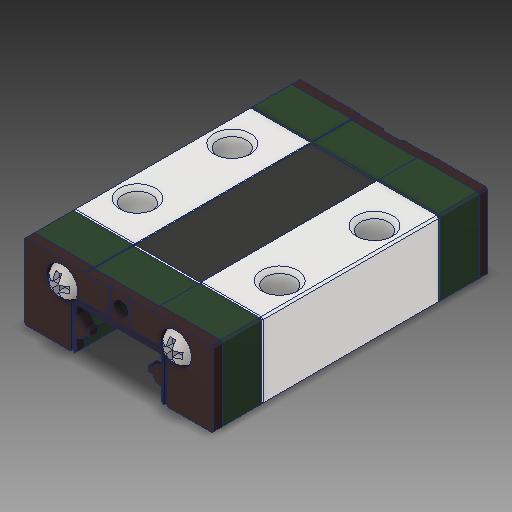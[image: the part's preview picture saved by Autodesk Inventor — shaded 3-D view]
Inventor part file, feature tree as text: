
AUTODESK INVENTOR PART (.ipt)
format: ipt  version: 2017.3 (Build 213256000, 256)  size: 610,304 bytes
history: imported  units: mm
features: other x7, sketch x2, plane x1, imported_body x1
ambient origin geometry x8: Origin, YZ Plane, XZ Plane, XY Plane, X Axis, Y Axis, Z Axis, Center Point
bodies: Solid1 (imported_parasolid), Solid2 (imported_parasolid), Solid3 (imported_parasolid), Solid4 (imported_parasolid), Solid5 (imported_parasolid)
feature tree (11):
  other  "MGN9C Block.ipt"
  other  "Solid1::MGN9C Block.ipt"
  other  "Solid2::MGN9C Block.ipt"
  other  "Solid3::MGN9C Block.ipt"
  other  "Solid4::MGN9C Block.ipt"
  other  "Solid9::MGN9C Block.ipt"
  other  "TaggingFeature1"
  sketch  "Sketch2"  dims[d0=10.0mm]
  sketch  "Sketch3"
  plane  "Work Plane1"
  imported_body  NMx_Import_Brep_tag  [imported B-rep: ~326 faces, bbox_mm=[20.0, 8.0, 30.285311]]
